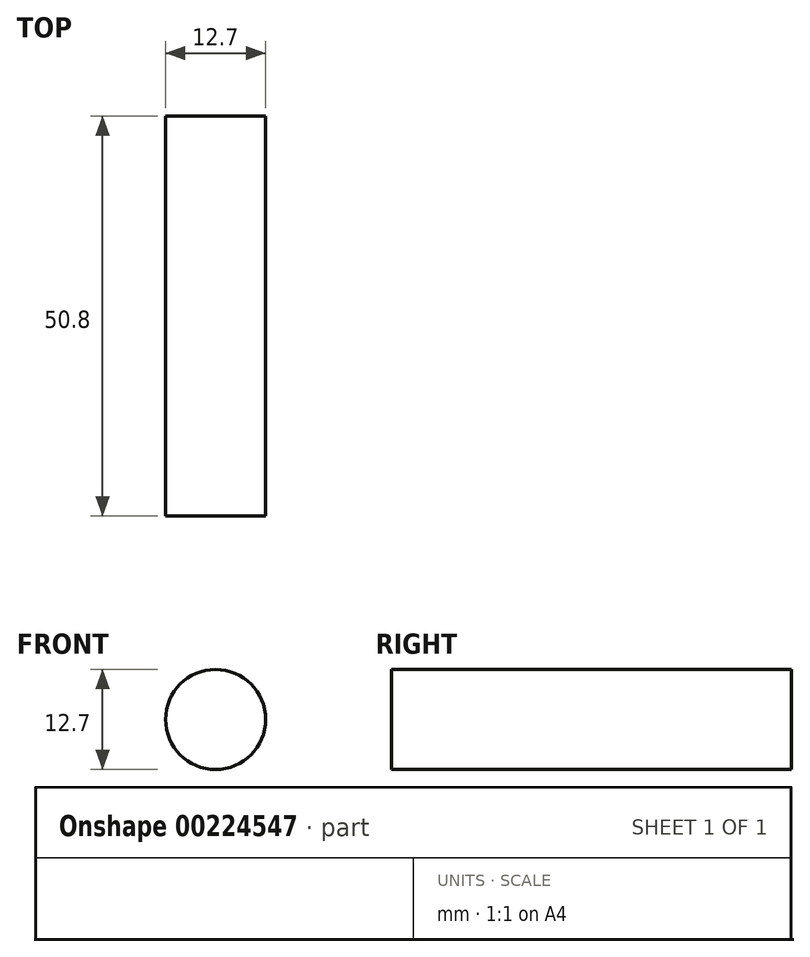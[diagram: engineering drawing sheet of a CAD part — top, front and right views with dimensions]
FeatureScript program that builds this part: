
annotation { "Feature Type Name" : "Feature", "Feature Type Description" : "" }
export const myFeature = defineFeature(function(context is Context, id is Id, definition is map)
    precondition{}
    {
        {
            var Q0;
            Q0=qCreatedBy(makeId("Front.planeOp"),FACE);
            var sketch = newSketch(context, id + "F0", { "sketchPlane" : qUnion([Q0])});
            skCircle(sketch, "E0", {"center": v(-60.46, 38.6) * mm, "radius": 6.35 * mm});
            skSolve(sketch);
        }
        {
            var Q0;
            Q0=makeQuery(id+"F0.imprint","IMPRINT",FACE,{"disambiguationData":[TD([[makeQuery(id+"F0.imprint","IMPRINT",EDGE,{"derivedFrom":sQuery(id+"F0.wireOp",EDGE,"E0")}),1.0]])]});
            extrude(context, id + "F1", {"entities" : qUnion([Q0]), "depth" : 50.8 * mm});
        }
    });
